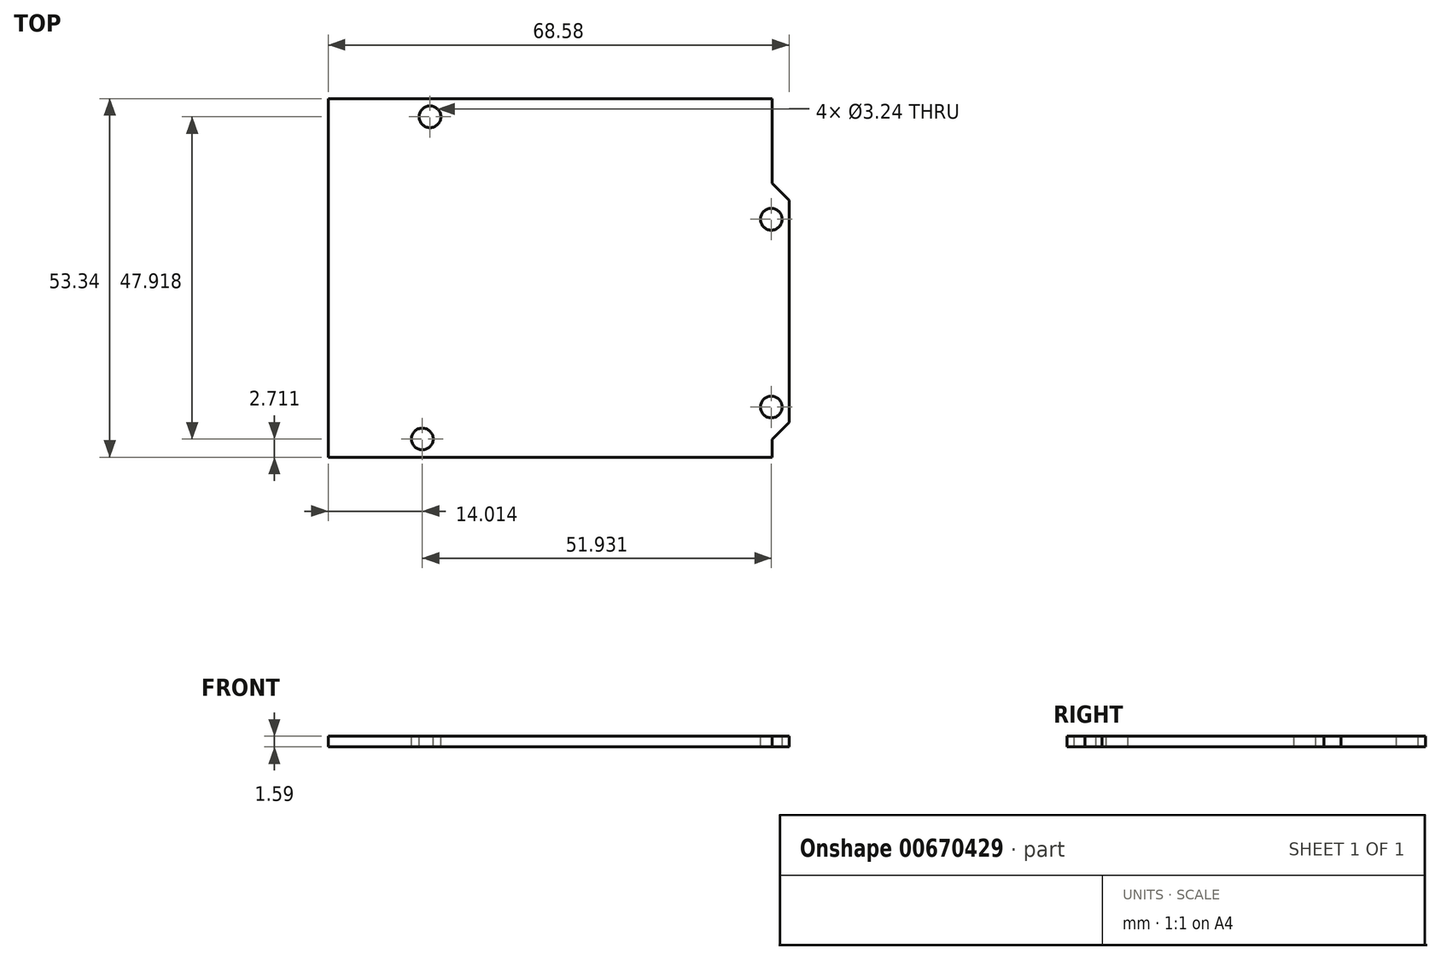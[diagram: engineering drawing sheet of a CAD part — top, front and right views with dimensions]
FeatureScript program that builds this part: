
annotation { "Feature Type Name" : "Feature", "Feature Type Description" : "" }
export const myFeature = defineFeature(function(context is Context, id is Id, definition is map)
    precondition{}
    {
        {
            var Q0;
            Q0=qCreatedBy(makeId("Top.planeOp"),FACE);
            var sketch = newSketch(context, id + "F0", { "sketchPlane" : qUnion([Q0])});
            skLineSegment(sketch, "E0", {"start": v(-33.02, 26.67) * mm, "end": v(33.02, 26.67) * mm});
            skLineSegment(sketch, "E1", {"start": v(33.02, 26.67) * mm, "end": v(33.02, 14.1) * mm});
            skLineSegment(sketch, "E2", {"start": v(33.02, -26.67) * mm, "end": v(-33.02, -26.67) * mm});
            skLineSegment(sketch, "E3", {"start": v(-33.02, -26.67) * mm, "end": v(-33.02, 26.67) * mm});
            skLineSegment(sketch, "E4", {"start": v(33.02, -24) * mm, "end": v(35.56, -21.46) * mm});
            skLineSegment(sketch, "E5", {"start": v(35.56, -21.46) * mm, "end": v(35.56, 11.56) * mm});
            skLineSegment(sketch, "E6", {"start": v(35.56, 11.56) * mm, "end": v(33.02, 14.1) * mm});
            skLineSegment(sketch, "E7.trimOffspring", {"start": v(33.02, -24) * mm, "end": v(33.02, -26.67) * mm});
            skSolve(sketch);
        }
        {
            var Q0;
            Q0 = qSketchRegion(id + "F0", true);
            extrude(context, id + "F1", {"entities" : qUnion([Q0]), "depth" : 1.59 * mm, "offsetDistance" : 25 * mm});
        }
        {
            var Q0;
            Q0=makeQuery(id+"F1.opExtrude","CAP_FACE",FACE,{"disambiguationData":[OSD([sQuery(id+"F0.wireOp",EDGE,"E0"),sQuery(id+"F0.wireOp",EDGE,"E1"),sQuery(id+"F0.wireOp",EDGE,"E2"),sQuery(id+"F0.wireOp",EDGE,"E3"),sQuery(id+"F0.wireOp",EDGE,"E4"),sQuery(id+"F0.wireOp",EDGE,"E5"),sQuery(id+"F0.wireOp",EDGE,"E6"),sQuery(id+"F0.wireOp",EDGE,"E7.trimOffspring")])],"isStart":false});
            var sketch = newSketch(context, id + "F2", { "sketchPlane" : qUnion([Q0])});
            skCircle(sketch, "E8", {"center": v(-17.86, 23.96) * mm, "radius": 1.62 * mm});
            skCircle(sketch, "E9", {"center": v(-19, -23.96) * mm, "radius": 1.62 * mm});
            skCircle(sketch, "E10", {"center": v(32.93, 8.72) * mm, "radius": 1.62 * mm});
            skCircle(sketch, "E11", {"center": v(32.93, -19.2) * mm, "radius": 1.62 * mm});
            skSolve(sketch);
        }
        {
            var Q0;
            Q0 = qSketchRegion(id + "F2", true);
            var Q1;
            Q1=makeQuery(id+"F1.opExtrude","SWEPT_BODY",BODY,{"disambiguationData":[OSD([sQuery(id+"F0.wireOp",EDGE,"E0"),sQuery(id+"F0.wireOp",EDGE,"E1"),sQuery(id+"F0.wireOp",EDGE,"E2"),sQuery(id+"F0.wireOp",EDGE,"E3"),sQuery(id+"F0.wireOp",EDGE,"E4"),sQuery(id+"F0.wireOp",EDGE,"E5"),sQuery(id+"F0.wireOp",EDGE,"E6"),sQuery(id+"F0.wireOp",EDGE,"E7.trimOffspring")])]});
            extrude(context, id + "F3", {"entities" : qUnion([Q0]), "operationType" : NewBodyOperationType.REMOVE, "endBound" : BoundingType.THROUGH_ALL, "oppositeDirection" : true, "depth" : 25 * mm, "endBoundEntityBody" : qUnion([Q1]), "offsetDistance" : 25 * mm});
        }
    });
